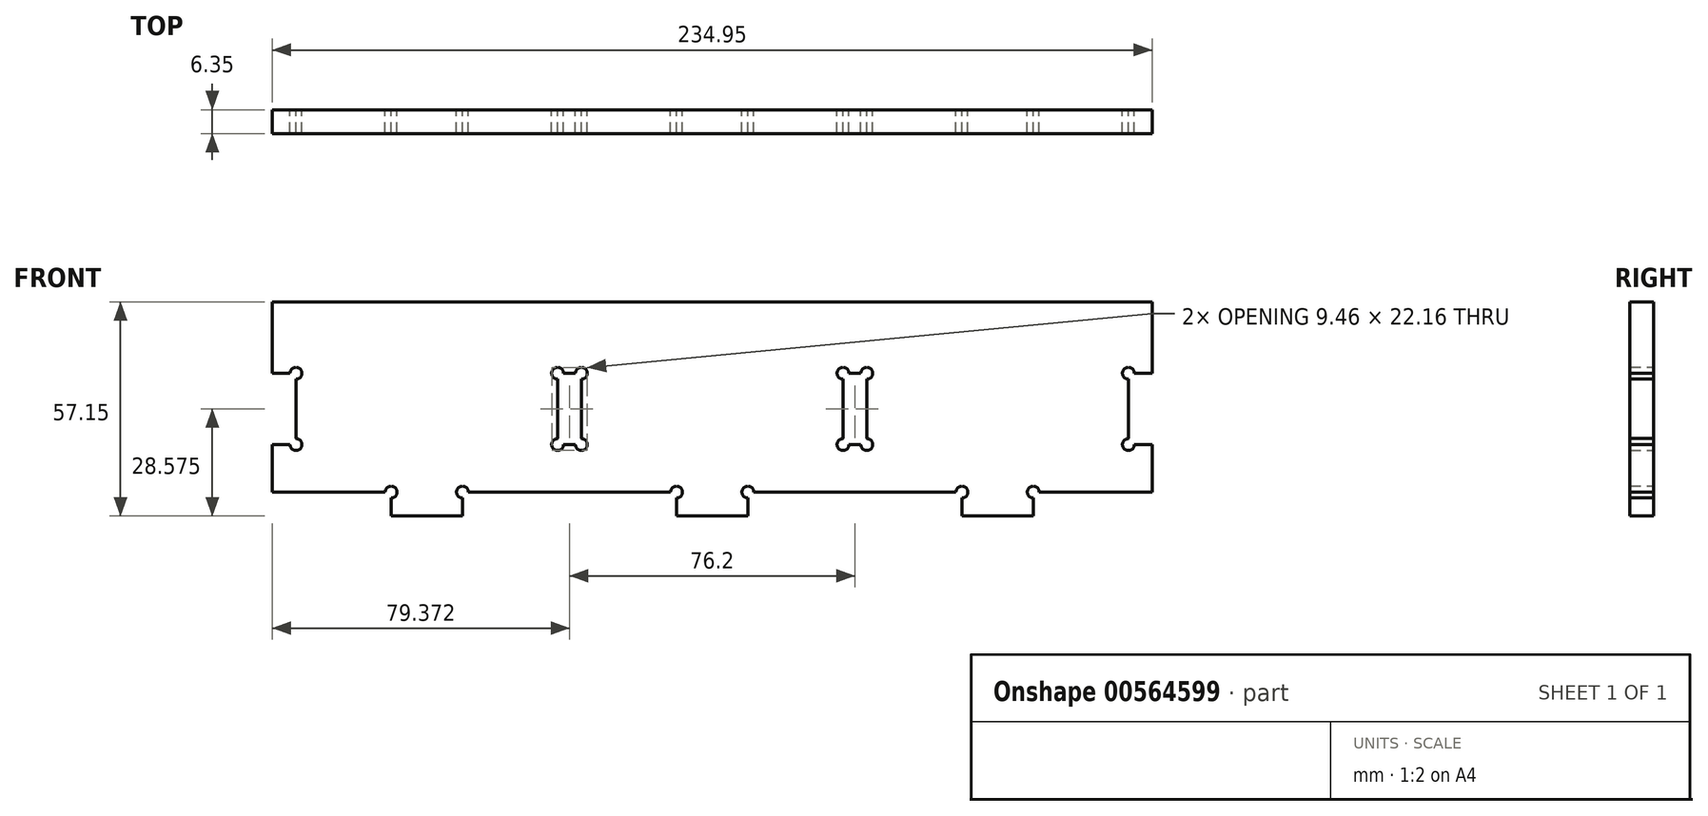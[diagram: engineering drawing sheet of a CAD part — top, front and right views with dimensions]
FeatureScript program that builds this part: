
annotation { "Feature Type Name" : "Feature", "Feature Type Description" : "" }
export const myFeature = defineFeature(function(context is Context, id is Id, definition is map)
    precondition{}
    {
        {
            var Q0;
            Q0=qCreatedBy(makeId("Front.planeOp"),FACE);
            var sketch = newSketch(context, id + "F0", { "sketchPlane" : qUnion([Q0])});
            skLineSegment(sketch, "E0.bottom", {"start": v(-79.86, 34.47) * mm, "end": v(155.09, 34.47) * mm});
            skLineSegment(sketch, "E0.top", {"start": v(-79.86, -16.33) * mm, "end": v(155.09, -16.33) * mm});
            skLineSegment(sketch, "E0.left", {"start": v(-79.86, 34.47) * mm, "end": v(-79.86, -16.33) * mm});
            skLineSegment(sketch, "E0.right", {"start": v(155.09, 34.47) * mm, "end": v(155.09, -16.33) * mm});
            skLineSegment(sketch, "E1.bottom", {"start": v(-3.66, 15.42) * mm, "end": v(2.69, 15.42) * mm});
            skLineSegment(sketch, "E1.top", {"start": v(-3.66, -3.63) * mm, "end": v(2.69, -3.63) * mm});
            skLineSegment(sketch, "E1.left", {"start": v(-3.66, 15.42) * mm, "end": v(-3.66, -3.63) * mm});
            skLineSegment(sketch, "E1.right", {"start": v(2.69, 15.42) * mm, "end": v(2.69, -3.63) * mm});
            skLineSegment(sketch, "E2.bottom", {"start": v(72.54, 15.42) * mm, "end": v(78.89, 15.42) * mm});
            skLineSegment(sketch, "E2.top", {"start": v(72.54, -3.63) * mm, "end": v(78.89, -3.63) * mm});
            skLineSegment(sketch, "E2.left", {"start": v(72.54, 15.42) * mm, "end": v(72.54, -3.63) * mm});
            skLineSegment(sketch, "E2.right", {"start": v(78.89, 15.42) * mm, "end": v(78.89, -3.63) * mm});
            skLineSegment(sketch, "E3.bottom", {"start": v(155.09, 15.42) * mm, "end": v(148.74, 15.42) * mm});
            skLineSegment(sketch, "E3.top", {"start": v(155.09, -3.63) * mm, "end": v(148.74, -3.63) * mm});
            skLineSegment(sketch, "E3.left", {"start": v(155.09, 15.42) * mm, "end": v(155.09, -3.63) * mm});
            skLineSegment(sketch, "E3.right", {"start": v(148.74, 15.42) * mm, "end": v(148.74, -3.63) * mm});
            skLineSegment(sketch, "E4.bottom", {"start": v(-79.86, 15.42) * mm, "end": v(-73.51, 15.42) * mm});
            skLineSegment(sketch, "E4.top", {"start": v(-79.86, -3.63) * mm, "end": v(-73.51, -3.63) * mm});
            skLineSegment(sketch, "E4.left", {"start": v(-79.86, 15.42) * mm, "end": v(-79.86, -3.63) * mm});
            skLineSegment(sketch, "E4.right", {"start": v(-73.51, 15.42) * mm, "end": v(-73.51, -3.63) * mm});
            skLineSegment(sketch, "E5.bottom", {"start": v(-48.11, -16.33) * mm, "end": v(-29.06, -16.33) * mm});
            skLineSegment(sketch, "E5.top", {"start": v(-48.11, -22.68) * mm, "end": v(-29.06, -22.68) * mm});
            skLineSegment(sketch, "E5.left", {"start": v(-48.11, -16.33) * mm, "end": v(-48.11, -22.68) * mm});
            skLineSegment(sketch, "E5.right", {"start": v(-29.06, -16.33) * mm, "end": v(-29.06, -22.68) * mm});
            skLineSegment(sketch, "E6.bottom", {"start": v(28.09, -16.33) * mm, "end": v(47.14, -16.33) * mm});
            skLineSegment(sketch, "E6.top", {"start": v(28.09, -22.68) * mm, "end": v(47.14, -22.68) * mm});
            skLineSegment(sketch, "E6.left", {"start": v(28.09, -16.33) * mm, "end": v(28.09, -22.68) * mm});
            skLineSegment(sketch, "E6.right", {"start": v(47.14, -16.33) * mm, "end": v(47.14, -22.68) * mm});
            skLineSegment(sketch, "E7.bottom", {"start": v(104.29, -16.33) * mm, "end": v(123.34, -16.33) * mm});
            skLineSegment(sketch, "E7.top", {"start": v(104.29, -22.68) * mm, "end": v(123.34, -22.68) * mm});
            skLineSegment(sketch, "E7.left", {"start": v(104.29, -16.33) * mm, "end": v(104.29, -22.68) * mm});
            skLineSegment(sketch, "E7.right", {"start": v(123.34, -16.33) * mm, "end": v(123.34, -22.68) * mm});
            skPoint(sketch, "E8.visualSharp", {"position": v(-73.51, 15.42) * mm});
            skLineSegment(sketch, "E8.filletArc", {"start": v(-73.51, 15.42) * mm, "end": v(-73.51, 15.42) * mm});
            skPoint(sketch, "E9.visualSharp", {"position": v(-73.51, -3.63) * mm});
            skLineSegment(sketch, "E9.filletArc", {"start": v(-73.51, -3.63) * mm, "end": v(-73.51, -3.63) * mm});
            skPoint(sketch, "E10.visualSharp", {"position": v(-3.66, 15.42) * mm});
            skLineSegment(sketch, "E10.filletArc", {"start": v(-3.66, 15.42) * mm, "end": v(-3.66, 15.42) * mm});
            skPoint(sketch, "E11.visualSharp", {"position": v(2.69, 15.42) * mm});
            skLineSegment(sketch, "E11.filletArc", {"start": v(2.69, 15.42) * mm, "end": v(2.69, 15.42) * mm});
            skPoint(sketch, "E12.visualSharp", {"position": v(2.69, -3.63) * mm});
            skLineSegment(sketch, "E12.filletArc", {"start": v(2.69, -3.63) * mm, "end": v(2.69, -3.63) * mm});
            skPoint(sketch, "E13.visualSharp", {"position": v(-3.66, -3.63) * mm});
            skLineSegment(sketch, "E13.filletArc", {"start": v(-3.66, -3.63) * mm, "end": v(-3.66, -3.63) * mm});
            skPoint(sketch, "E14.visualSharp", {"position": v(-48.11, -22.68) * mm});
            skLineSegment(sketch, "E14.filletArc", {"start": v(-48.11, -22.68) * mm, "end": v(-48.11, -22.68) * mm});
            skPoint(sketch, "E15.visualSharp", {"position": v(-29.06, -22.68) * mm});
            skLineSegment(sketch, "E15.filletArc", {"start": v(-29.06, -22.68) * mm, "end": v(-29.06, -22.68) * mm});
            skPoint(sketch, "E16.visualSharp", {"position": v(72.54, 15.42) * mm});
            skLineSegment(sketch, "E16.filletArc", {"start": v(72.54, 15.42) * mm, "end": v(72.54, 15.42) * mm});
            skPoint(sketch, "E17.visualSharp", {"position": v(78.89, 15.42) * mm});
            skLineSegment(sketch, "E17.filletArc", {"start": v(78.89, 15.42) * mm, "end": v(78.89, 15.42) * mm});
            skPoint(sketch, "E18.visualSharp", {"position": v(78.89, -3.63) * mm});
            skLineSegment(sketch, "E18.filletArc", {"start": v(78.89, -3.63) * mm, "end": v(78.89, -3.63) * mm});
            skPoint(sketch, "E19.visualSharp", {"position": v(72.54, -3.63) * mm});
            skLineSegment(sketch, "E19.filletArc", {"start": v(72.54, -3.63) * mm, "end": v(72.54, -3.63) * mm});
            skPoint(sketch, "E20.visualSharp", {"position": v(47.14, -22.68) * mm});
            skLineSegment(sketch, "E20.filletArc", {"start": v(47.14, -22.68) * mm, "end": v(47.14, -22.68) * mm});
            skPoint(sketch, "E21.visualSharp", {"position": v(28.09, -22.68) * mm});
            skLineSegment(sketch, "E21.filletArc", {"start": v(28.09, -22.68) * mm, "end": v(28.09, -22.68) * mm});
            skPoint(sketch, "E22.visualSharp", {"position": v(104.29, -22.68) * mm});
            skLineSegment(sketch, "E22.filletArc", {"start": v(104.29, -22.68) * mm, "end": v(104.29, -22.68) * mm});
            skPoint(sketch, "E23.visualSharp", {"position": v(123.34, -22.68) * mm});
            skLineSegment(sketch, "E23.filletArc", {"start": v(123.34, -22.68) * mm, "end": v(123.34, -22.68) * mm});
            skPoint(sketch, "E24.visualSharp", {"position": v(148.74, 15.42) * mm});
            skLineSegment(sketch, "E24.filletArc", {"start": v(148.74, 15.42) * mm, "end": v(148.74, 15.42) * mm});
            skPoint(sketch, "E25.visualSharp", {"position": v(148.74, -3.63) * mm});
            skLineSegment(sketch, "E25.filletArc", {"start": v(148.74, -3.63) * mm, "end": v(148.74, -3.63) * mm});
            skCircle(sketch, "E26", {"center": v(-48.11, -16.33) * mm, "radius": 0.72 * mm});
            skCircle(sketch, "E27", {"center": v(-73.51, 15.42) * mm, "radius": 1.59 * mm});
            skCircle(sketch, "E28", {"center": v(-73.51, -3.63) * mm, "radius": 1.59 * mm});
            skCircle(sketch, "E29", {"center": v(-3.66, 15.42) * mm, "radius": 1.59 * mm});
            skCircle(sketch, "E30", {"center": v(2.69, 15.42) * mm, "radius": 1.59 * mm});
            skCircle(sketch, "E31", {"center": v(2.69, -3.63) * mm, "radius": 1.59 * mm});
            skCircle(sketch, "E32", {"center": v(-3.66, -3.63) * mm, "radius": 1.59 * mm});
            skCircle(sketch, "E33", {"center": v(-29.06, -16.33) * mm, "radius": 1.59 * mm});
            skCircle(sketch, "E34", {"center": v(-48.11, -16.33) * mm, "radius": 1.59 * mm});
            skCircle(sketch, "E35", {"center": v(72.54, 15.42) * mm, "radius": 1.59 * mm});
            skCircle(sketch, "E36", {"center": v(78.89, 15.42) * mm, "radius": 1.59 * mm});
            skCircle(sketch, "E37", {"center": v(78.89, -3.63) * mm, "radius": 1.59 * mm});
            skCircle(sketch, "E38", {"center": v(104.29, -16.33) * mm, "radius": 1.59 * mm});
            skCircle(sketch, "E39", {"center": v(123.34, -16.33) * mm, "radius": 1.59 * mm});
            skCircle(sketch, "E40", {"center": v(72.54, -3.63) * mm, "radius": 1.59 * mm});
            skCircle(sketch, "E41", {"center": v(148.74, 15.42) * mm, "radius": 1.59 * mm});
            skCircle(sketch, "E42", {"center": v(148.74, -3.63) * mm, "radius": 1.59 * mm});
            skCircle(sketch, "E43", {"center": v(47.14, -16.33) * mm, "radius": 1.59 * mm});
            skCircle(sketch, "E44", {"center": v(28.09, -16.33) * mm, "radius": 1.59 * mm});
            skSolve(sketch);
        }
        {
            var Q0;
            {var subQ61=sQuery(id+"F0.wireOp",EDGE,"E0.bottom");Q0=makeQuery(id+"F0.imprint","IMPRINT",FACE,{"disambiguationData":[TD([[makeQuery(id+"F0.imprint","IMPRINT",EDGE,{"derivedFrom":subQ61}),-1.0]])]});}
            var Q1;
            {var subQ1=sQuery(id+"F0.wireOp",EDGE,"E5.top");Q1=makeQuery(id+"F0.imprint","IMPRINT",FACE,{"disambiguationData":[TD([[makeQuery(id+"F0.imprint","IMPRINT",EDGE,{"derivedFrom":subQ1}),1.0]])]});}
            var Q2;
            {var subQ1=sQuery(id+"F0.wireOp",EDGE,"E6.top");Q2=makeQuery(id+"F0.imprint","IMPRINT",FACE,{"disambiguationData":[TD([[makeQuery(id+"F0.imprint","IMPRINT",EDGE,{"derivedFrom":subQ1}),1.0]])]});}
            var Q3;
            {var subQ1=sQuery(id+"F0.wireOp",EDGE,"E7.top");Q3=makeQuery(id+"F0.imprint","IMPRINT",FACE,{"disambiguationData":[TD([[makeQuery(id+"F0.imprint","IMPRINT",EDGE,{"derivedFrom":subQ1}),1.0]])]});}
            extrude(context, id + "F1", {"entities" : qUnion([Q0, Q1, Q2, Q3]), "depth" : 6.35 * mm, "offsetDistance" : 25.4 * mm});
        }
    });
